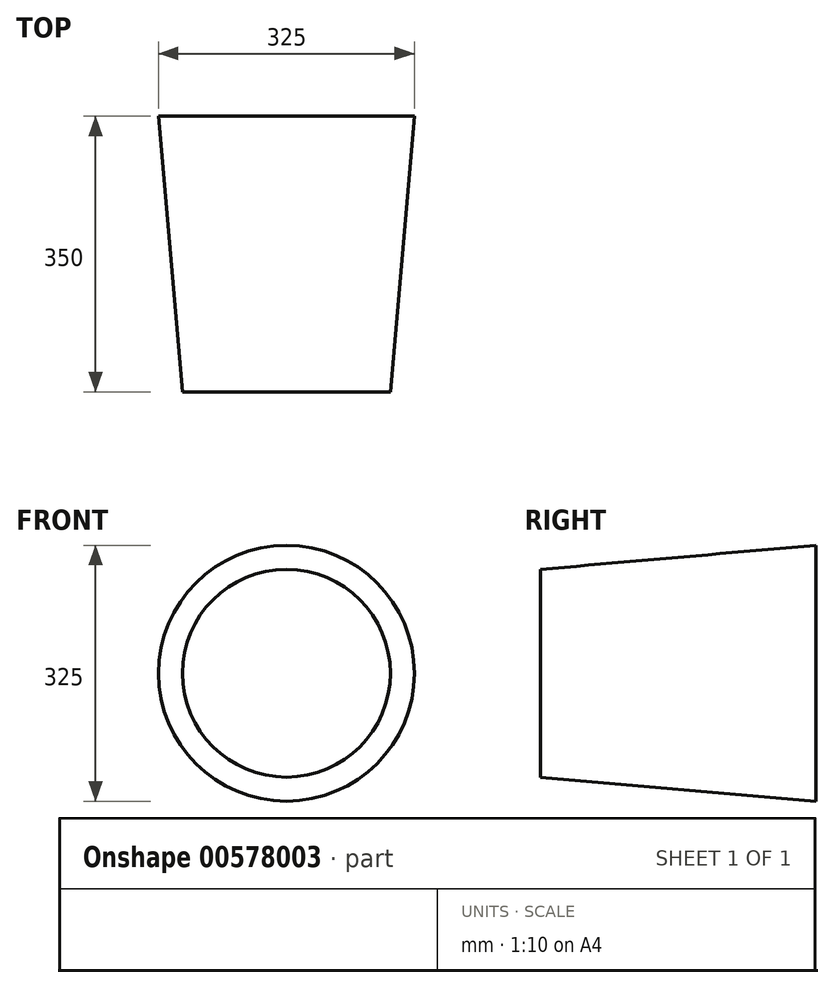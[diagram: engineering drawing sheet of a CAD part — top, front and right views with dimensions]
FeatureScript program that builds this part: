
annotation { "Feature Type Name" : "Feature", "Feature Type Description" : "" }
export const myFeature = defineFeature(function(context is Context, id is Id, definition is map)
    precondition{}
    {
        {
            var Q0;
            Q0=qCreatedBy(makeId("Top.planeOp"),FACE);
            var sketch = newSketch(context, id + "F0", { "sketchPlane" : qUnion([Q0])});
            skLineSegment(sketch, "E0", {"start": v(0, 175.1) * mm, "end": v(0, -174.9) * mm});
            skLineSegment(sketch, "E1", {"start": v(0, -174.9) * mm, "end": v(132, -174.9) * mm});
            skLineSegment(sketch, "E2", {"start": v(132, -174.9) * mm, "end": v(162.5, 175.1) * mm});
            skLineSegment(sketch, "E3", {"start": v(162.5, 175.1) * mm, "end": v(0, 175.1) * mm});
            skSolve(sketch);
        }
        {
            var Q0;
            Q0 = qSketchRegion(id + "F0", true);
            var Q1;
            Q1=sQuery(id+"F0.wireOp",EDGE,"E0");
            revolve(context, id + "F1", {"entities" : qUnion([Q0]), "axis" : qUnion([Q1]), "revolveType" : RevolveType.FULL});
        }
    });
